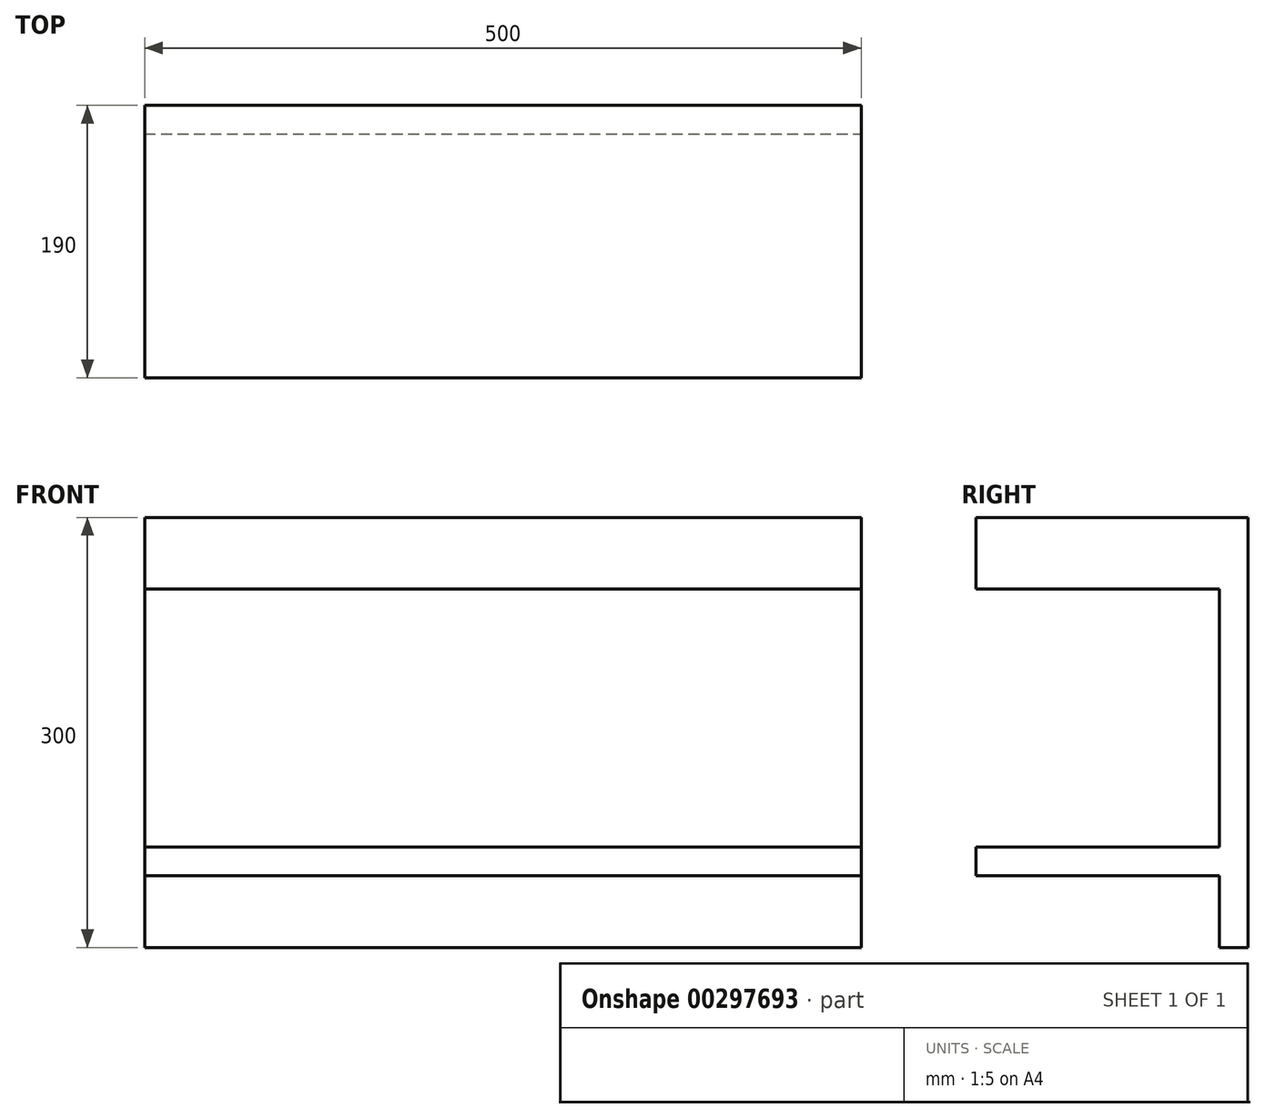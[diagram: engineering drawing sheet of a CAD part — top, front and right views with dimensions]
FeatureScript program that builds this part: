
annotation { "Feature Type Name" : "Feature", "Feature Type Description" : "" }
export const myFeature = defineFeature(function(context is Context, id is Id, definition is map)
    precondition{}
    {
        {
            var Q0;
            Q0=qCreatedBy(makeId("Top.planeOp"),FACE);
            var sketch = newSketch(context, id + "F0", { "sketchPlane" : qUnion([Q0])});
            skLineSegment(sketch, "E0", {"start": v(0, 0) * mm, "end": v(250, 0) * mm, "construction": true});
            skLineSegment(sketch, "E1.bottom", {"start": v(250, 0) * mm, "end": v(-250, 0) * mm});
            skLineSegment(sketch, "E1.top", {"start": v(250, -190) * mm, "end": v(-250, -190) * mm});
            skLineSegment(sketch, "E1.left", {"start": v(250, 0) * mm, "end": v(250, -190) * mm});
            skLineSegment(sketch, "E1.right", {"start": v(-250, 0) * mm, "end": v(-250, -190) * mm});
            skSolve(sketch);
        }
        {
            var Q0;
            Q0=makeQuery(id+"F0.imprint","IMPRINT",FACE,{"disambiguationData":[TD([[makeQuery(id+"F0.imprint","IMPRINT",EDGE,{"derivedFrom":sQuery(id+"F0.wireOp",EDGE,"E1.bottom")}),1.0]])]});
            extrude(context, id + "F1", {"entities" : qUnion([Q0]), "oppositeDirection" : true, "depth" : 50 * mm});
        }
        {
            var Q0;
            Q0=qCreatedBy(makeId("Front.planeOp"),FACE);
            var sketch = newSketch(context, id + "F2", { "sketchPlane" : qUnion([Q0])});
            skLineSegment(sketch, "E2", {"start": v(0, 0) * mm, "end": v(0, -300) * mm, "construction": true});
            skLineSegment(sketch, "E3", {"start": v(0, -300) * mm, "end": v(250, -300) * mm, "construction": true});
            skLineSegment(sketch, "E4", {"start": v(0, 0) * mm, "end": v(-250, 0) * mm, "construction": true});
            skLineSegment(sketch, "E5.bottom", {"start": v(250, -300) * mm, "end": v(-250, -300) * mm});
            skLineSegment(sketch, "E5.top", {"start": v(250, 0) * mm, "end": v(-250, 0) * mm});
            skLineSegment(sketch, "E5.left", {"start": v(250, -300) * mm, "end": v(250, 0) * mm});
            skLineSegment(sketch, "E5.right", {"start": v(-250, -300) * mm, "end": v(-250, 0) * mm});
            skSolve(sketch);
        }
        {
            var Q0;
            Q0=makeQuery(id+"F2.imprint","IMPRINT",FACE,{"disambiguationData":[TD([[makeQuery(id+"F2.imprint","IMPRINT",EDGE,{"derivedFrom":sQuery(id+"F2.wireOp",EDGE,"E5.bottom")}),-1.0]])]});
            extrude(context, id + "F3", {"entities" : qUnion([Q0]), "operationType" : NewBodyOperationType.ADD, "depth" : 20 * mm});
        }
        {
            var Q0;
            Q0=makeQuery(id+"F3.opExtrude","CAP_FACE",FACE,{"disambiguationData":[OSD([sQuery(id+"F2.wireOp",EDGE,"E5.bottom"),sQuery(id+"F2.wireOp",EDGE,"E5.top"),sQuery(id+"F2.wireOp",EDGE,"E5.left"),sQuery(id+"F2.wireOp",EDGE,"E5.right")])],"isStart":false});
            var sketch = newSketch(context, id + "F4", { "sketchPlane" : qUnion([Q0])});
            skLineSegment(sketch, "E6", {"start": v(0, -50) * mm, "end": v(0, -240) * mm, "construction": true});
            skPoint(sketch, "E6.startSnap0", {"position": v(0, -50) * mm});
            skLineSegment(sketch, "E7.bottom", {"start": v(-250, -250) * mm, "end": v(250, -250) * mm});
            skLineSegment(sketch, "E7.top", {"start": v(-250, -230) * mm, "end": v(250, -230) * mm});
            skLineSegment(sketch, "E7.left", {"start": v(-250, -250) * mm, "end": v(-250, -230) * mm});
            skLineSegment(sketch, "E7.right", {"start": v(250, -250) * mm, "end": v(250, -230) * mm});
            skPoint(sketch, "E7.middle", {"position": v(0, -240) * mm});
            skSolve(sketch);
        }
        {
            var Q0;
            Q0=makeQuery(id+"F4.imprint","IMPRINT",FACE,{"disambiguationData":[TD([[makeQuery(id+"F4.imprint","IMPRINT",EDGE,{"derivedFrom":sQuery(id+"F4.wireOp",EDGE,"E7.bottom")}),1.0]])]});
            extrude(context, id + "F5", {"entities" : qUnion([Q0]), "operationType" : NewBodyOperationType.ADD, "depth" : 170 * mm});
        }
        {
            var Q0;
            {var subQ0=sQuery(id+"F4.wireOp",EDGE,"E7.top");Q0=makeQuery(id+"F4.imprint","IMPRINT",FACE,{"disambiguationData":[TD([[makeQuery(id+"F4.imprint","IMPRINT",EDGE,{"derivedFrom":subQ0}),1.0]])]});}
            var sketch = newSketch(context, id + "F6", { "sketchPlane" : qUnion([Q0])});
            skLineSegment(sketch, "E8", {"start": v(0, -50) * mm, "end": v(230, -50) * mm, "construction": true});
            skLineSegment(sketch, "E9", {"start": v(0, -230) * mm, "end": v(230, -230) * mm, "construction": true});
            skLineSegment(sketch, "E10", {"start": v(0, -50) * mm, "end": v(-230, -50) * mm, "construction": true});
            skLineSegment(sketch, "E11", {"start": v(0, -230) * mm, "end": v(-230, -230) * mm, "construction": true});
            skLineSegment(sketch, "E12.bottom", {"start": v(-230, -50) * mm, "end": v(-250, -50) * mm});
            skLineSegment(sketch, "E12.top", {"start": v(-230, -230) * mm, "end": v(-250, -230) * mm});
            skLineSegment(sketch, "E12.left", {"start": v(-230, -50) * mm, "end": v(-230, -230) * mm});
            skLineSegment(sketch, "E12.right", {"start": v(-250, -50) * mm, "end": v(-250, -230) * mm});
            skLineSegment(sketch, "E13.bottom", {"start": v(230, -50) * mm, "end": v(250, -50) * mm});
            skLineSegment(sketch, "E13.top", {"start": v(230, -230) * mm, "end": v(250, -230) * mm});
            skLineSegment(sketch, "E13.left", {"start": v(230, -50) * mm, "end": v(230, -230) * mm});
            skLineSegment(sketch, "E13.right", {"start": v(250, -50) * mm, "end": v(250, -230) * mm});
            skSolve(sketch);
        }
        {
            var Q0;
            Q0=sQuery(id+"F6.wireOp",EDGE,"E12.right");
            var Q1;
            Q1=sQuery(id+"F6.wireOp",EDGE,"E12.left");
            var Q2;
            Q2=sQuery(id+"F6.wireOp",EDGE,"E12.bottom");
            var Q3;
            Q3=sQuery(id+"F6.wireOp",EDGE,"E12.top");
            var Q4;
            Q4=sQuery(id+"F6.wireOp",EDGE,"E13.left");
            var Q5;
            Q5=sQuery(id+"F6.wireOp",EDGE,"E13.right");
            var Q6;
            Q6=sQuery(id+"F6.wireOp",EDGE,"E13.top");
            var Q7;
            Q7=sQuery(id+"F6.wireOp",EDGE,"E13.bottom");
            extrude(context, id + "F7", {"bodyType" : ExtendedToolBodyType.SURFACE, "surfaceEntities" : qUnion([Q0, Q1, Q2, Q3, Q4, Q5, Q6, Q7]), "depth" : 170 * mm});
        }
        {
            var Q0;
            {var subQ0=sQuery(id+"F4.wireOp",EDGE,"E7.top");Q0=makeQuery(id+"F4.imprint","IMPRINT",FACE,{"disambiguationData":[TD([[makeQuery(id+"F4.imprint","IMPRINT",EDGE,{"derivedFrom":subQ0}),1.0]])]});}
            var sketch = newSketch(context, id + "F8", { "sketchPlane" : qUnion([Q0])});
            skLineSegment(sketch, "E14", {"start": v(-70, -50) * mm, "end": v(0, -50) * mm, "construction": true});
            skLineSegment(sketch, "E15", {"start": v(0, -50) * mm, "end": v(70, -50) * mm, "construction": true});
            skLineSegment(sketch, "E16.bottom", {"start": v(-70, -50) * mm, "end": v(-90, -50) * mm});
            skLineSegment(sketch, "E16.top", {"start": v(-70, -230) * mm, "end": v(-90, -230) * mm});
            skLineSegment(sketch, "E16.left", {"start": v(-70, -50) * mm, "end": v(-70, -230) * mm});
            skLineSegment(sketch, "E16.right", {"start": v(-90, -50) * mm, "end": v(-90, -230) * mm});
            skLineSegment(sketch, "E17.bottom", {"start": v(70, -50) * mm, "end": v(90, -50) * mm});
            skLineSegment(sketch, "E17.top", {"start": v(70, -230) * mm, "end": v(90, -230) * mm});
            skLineSegment(sketch, "E17.left", {"start": v(70, -50) * mm, "end": v(70, -230) * mm});
            skLineSegment(sketch, "E17.right", {"start": v(90, -50) * mm, "end": v(90, -230) * mm});
            skSolve(sketch);
        }
        {
            var Q0;
            Q0=sQuery(id+"F8.wireOp",EDGE,"E16.right");
            var Q1;
            Q1=sQuery(id+"F8.wireOp",EDGE,"E16.left");
            var Q2;
            Q2=sQuery(id+"F8.wireOp",EDGE,"E16.bottom");
            var Q3;
            Q3=sQuery(id+"F8.wireOp",EDGE,"E16.top");
            var Q4;
            Q4=sQuery(id+"F8.wireOp",EDGE,"E17.left");
            var Q5;
            Q5=sQuery(id+"F8.wireOp",EDGE,"E17.right");
            var Q6;
            Q6=sQuery(id+"F8.wireOp",EDGE,"E17.bottom");
            var Q7;
            Q7=sQuery(id+"F8.wireOp",EDGE,"E17.top");
            extrude(context, id + "F9", {"bodyType" : ExtendedToolBodyType.SURFACE, "surfaceEntities" : qUnion([Q0, Q1, Q2, Q3, Q4, Q5, Q6, Q7]), "depth" : 170 * mm});
        }
    });
